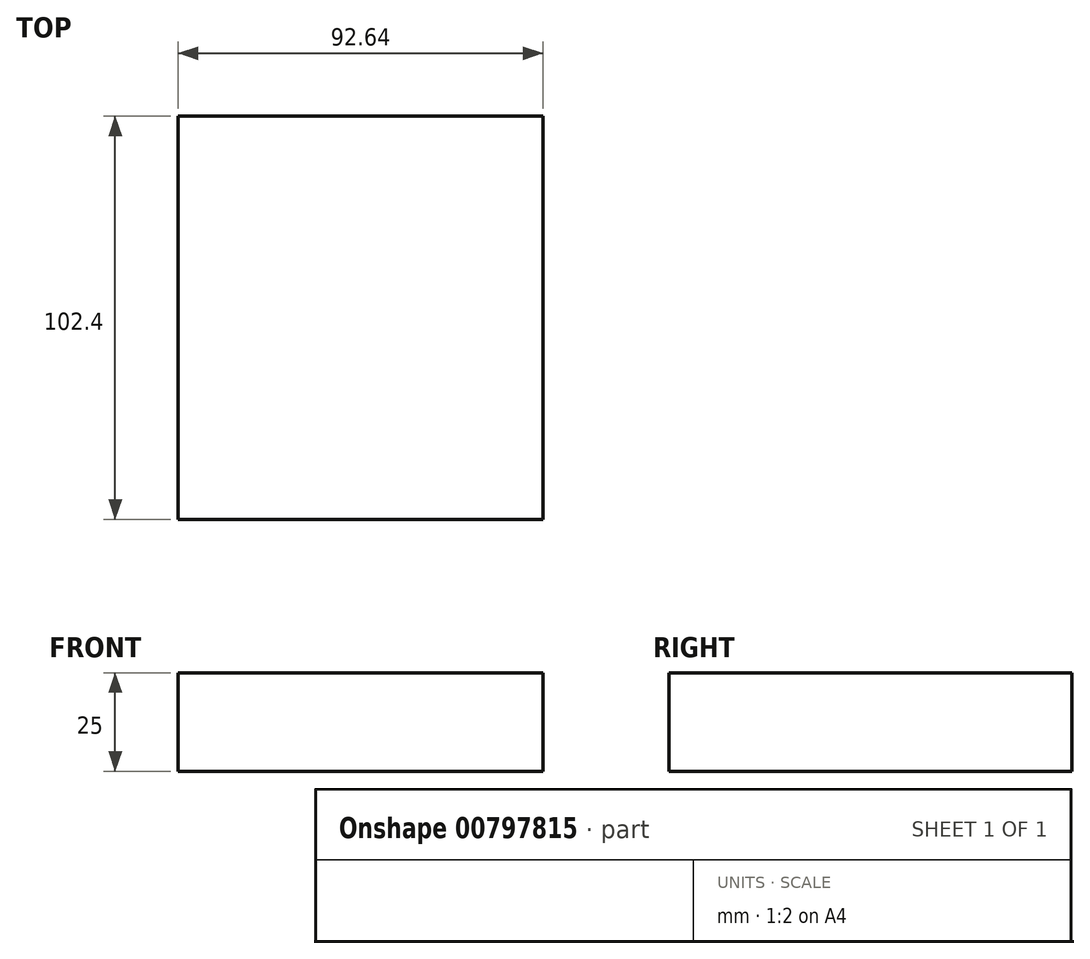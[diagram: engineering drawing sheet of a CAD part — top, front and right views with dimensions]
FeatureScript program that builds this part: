
annotation { "Feature Type Name" : "Feature", "Feature Type Description" : "" }
export const myFeature = defineFeature(function(context is Context, id is Id, definition is map)
    precondition{}
    {
        {
            var Q0;
            Q0=qCreatedBy(makeId("Top.planeOp"),FACE);
            var sketch = newSketch(context, id + "F0", { "sketchPlane" : qUnion([Q0])});
            skLineSegment(sketch, "E0.bottom", {"start": v(46.32, -51.2) * mm, "end": v(-46.32, -51.2) * mm});
            skLineSegment(sketch, "E0.top", {"start": v(46.32, 51.2) * mm, "end": v(-46.32, 51.2) * mm});
            skLineSegment(sketch, "E0.left", {"start": v(46.32, -51.2) * mm, "end": v(46.32, 51.2) * mm});
            skLineSegment(sketch, "E0.right", {"start": v(-46.32, -51.2) * mm, "end": v(-46.32, 51.2) * mm});
            skPoint(sketch, "E0.middle", {"position": v(0, 0) * mm});
            skSolve(sketch);
        }
        {
            var Q0;
            Q0 = qSketchRegion(id + "F0", true);
            extrude(context, id + "F1", {"entities" : qUnion([Q0]), "endBound" : BoundingType.SYMMETRIC, "depth" : 25 * mm, "offsetDistance" : 25 * mm});
        }
    });
